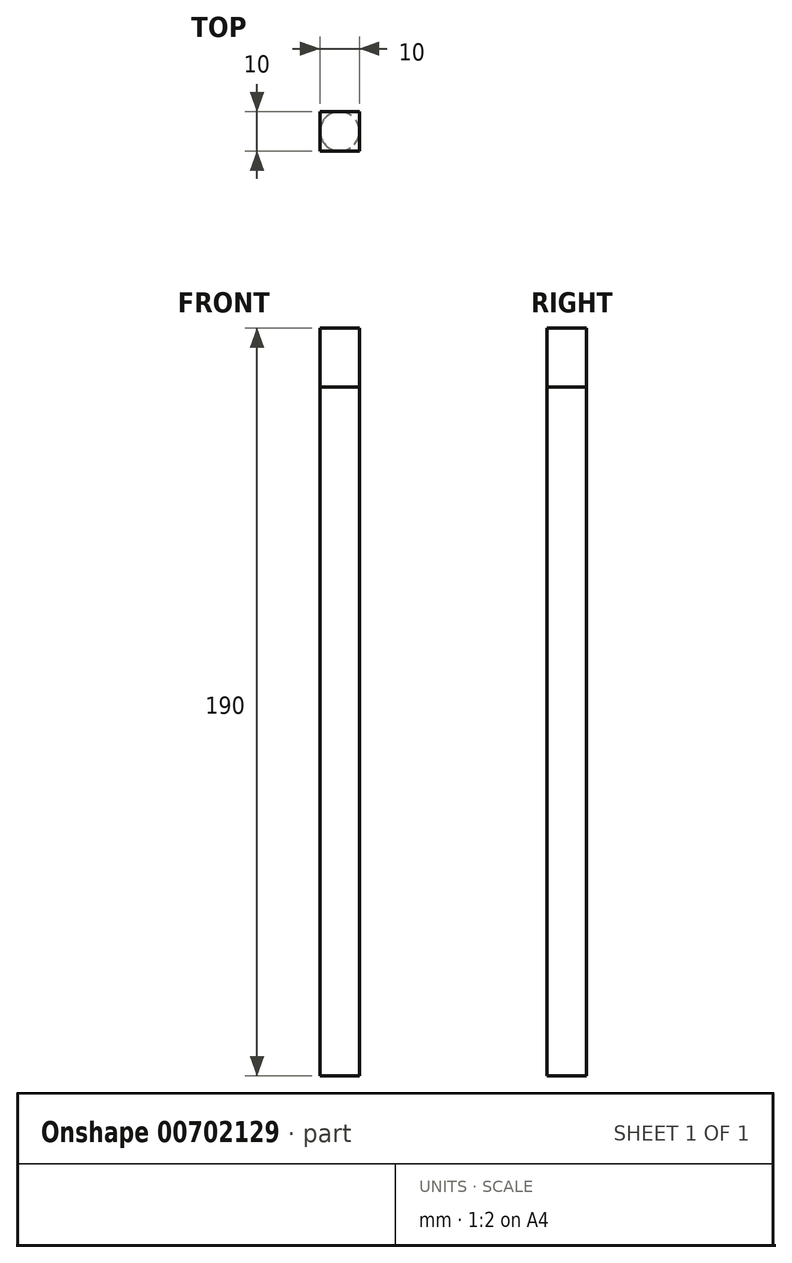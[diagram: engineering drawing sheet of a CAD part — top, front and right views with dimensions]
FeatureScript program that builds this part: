
annotation { "Feature Type Name" : "Feature", "Feature Type Description" : "" }
export const myFeature = defineFeature(function(context is Context, id is Id, definition is map)
    precondition{}
    {
        {
            var Q0;
            Q0=qCreatedBy(makeId("Top.planeOp"),FACE);
            var sketch = newSketch(context, id + "F0", { "sketchPlane" : qUnion([Q0])});
            skCircle(sketch, "E0", {"center": v(0, 0) * mm, "radius": 5 * mm});
            skSolve(sketch);
        }
        {
            var Q0;
            Q0=makeQuery(id+"F0.imprint","IMPRINT",FACE,{"disambiguationData":[TD([[makeQuery(id+"F0.imprint","IMPRINT",EDGE,{"derivedFrom":sQuery(id+"F0.wireOp",EDGE,"E0")}),1.0]])]});
            extrude(context, id + "F1", {"entities" : qUnion([Q0]), "depth" : 175 * mm, "offsetDistance" : 25 * mm});
        }
        {
            var Q0;
            Q0=makeQuery(id+"F1.opExtrude","CAP_FACE",FACE,{"disambiguationData":[OSD([sQuery(id+"F0.wireOp",EDGE,"E0")])],"isStart":false});
            var sketch = newSketch(context, id + "F2", { "sketchPlane" : qUnion([Q0])});
            skLineSegment(sketch, "E1.bottom", {"start": v(5, 5) * mm, "end": v(-5, 5) * mm});
            skLineSegment(sketch, "E1.top", {"start": v(5, -5) * mm, "end": v(-5, -5) * mm});
            skLineSegment(sketch, "E1.left", {"start": v(5, 5) * mm, "end": v(5, -5) * mm});
            skLineSegment(sketch, "E1.right", {"start": v(-5, 5) * mm, "end": v(-5, -5) * mm});
            skPoint(sketch, "E1.middle", {"position": v(0, 0) * mm});
            skSolve(sketch);
        }
        {
            var Q0;
            {var subQ0=makeQuery(id+"F1.opExtrude","CAP_EDGE",EDGE,{"disambiguationData":[OSD([sQuery(id+"F0.wireOp",EDGE,"E0")])],"isStart":false});var subQ1=makeQuery(id+"F2.imprint","INTERSECT",VERTEX,{"derivedFrom":[subQ0,sQuery(id+"F2.wireOp",EDGE,"E1.bottom")]});Q0=makeQuery(id+"F2.imprint","IMPRINT",FACE,{"disambiguationData":[TD([[makeQuery(id+"F2.imprint","IMPRINT",EDGE,{"disambiguationData":[TD([[subQ1,1.0]])],"derivedFrom":subQ0}),1.0]])]});}
            var Q1;
            {var subQ0=sQuery(id+"F2.wireOp",EDGE,"E1.left");var subQ1=sQuery(id+"F2.wireOp",EDGE,"E1.bottom");var subQ2=makeQuery(id+"F2.imprint","INTERSECT",VERTEX,{"derivedFrom":[subQ1,subQ0]});Q1=makeQuery(id+"F2.imprint","IMPRINT",FACE,{"disambiguationData":[TD([[makeQuery(id+"F2.imprint","IMPRINT",EDGE,{"disambiguationData":[TD([[subQ2,-1.0]])],"derivedFrom":subQ1}),1.0]])]});}
            var Q2;
            {var subQ0=sQuery(id+"F2.wireOp",EDGE,"E1.left");var subQ1=sQuery(id+"F2.wireOp",EDGE,"E1.top");var subQ2=makeQuery(id+"F2.imprint","INTERSECT",VERTEX,{"derivedFrom":[subQ1,subQ0]});Q2=makeQuery(id+"F2.imprint","IMPRINT",FACE,{"disambiguationData":[TD([[makeQuery(id+"F2.imprint","IMPRINT",EDGE,{"disambiguationData":[TD([[subQ2,-1.0]])],"derivedFrom":subQ1}),-1.0]])]});}
            var Q3;
            {var subQ0=sQuery(id+"F2.wireOp",EDGE,"E1.right");var subQ1=sQuery(id+"F2.wireOp",EDGE,"E1.top");var subQ2=makeQuery(id+"F2.imprint","INTERSECT",VERTEX,{"derivedFrom":[subQ1,subQ0]});Q3=makeQuery(id+"F2.imprint","IMPRINT",FACE,{"disambiguationData":[TD([[makeQuery(id+"F2.imprint","IMPRINT",EDGE,{"disambiguationData":[TD([[subQ2,1.0]])],"derivedFrom":subQ1}),-1.0]])]});}
            var Q4;
            {var subQ0=sQuery(id+"F2.wireOp",EDGE,"E1.right");var subQ1=sQuery(id+"F2.wireOp",EDGE,"E1.bottom");var subQ2=makeQuery(id+"F2.imprint","INTERSECT",VERTEX,{"derivedFrom":[subQ1,subQ0]});Q4=makeQuery(id+"F2.imprint","IMPRINT",FACE,{"disambiguationData":[TD([[makeQuery(id+"F2.imprint","IMPRINT",EDGE,{"disambiguationData":[TD([[subQ2,1.0]])],"derivedFrom":subQ1}),1.0]])]});}
            extrude(context, id + "F3", {"entities" : qUnion([Q0, Q1, Q2, Q3, Q4]), "operationType" : NewBodyOperationType.ADD, "depth" : 15 * mm, "offsetDistance" : 25 * mm});
        }
    });
